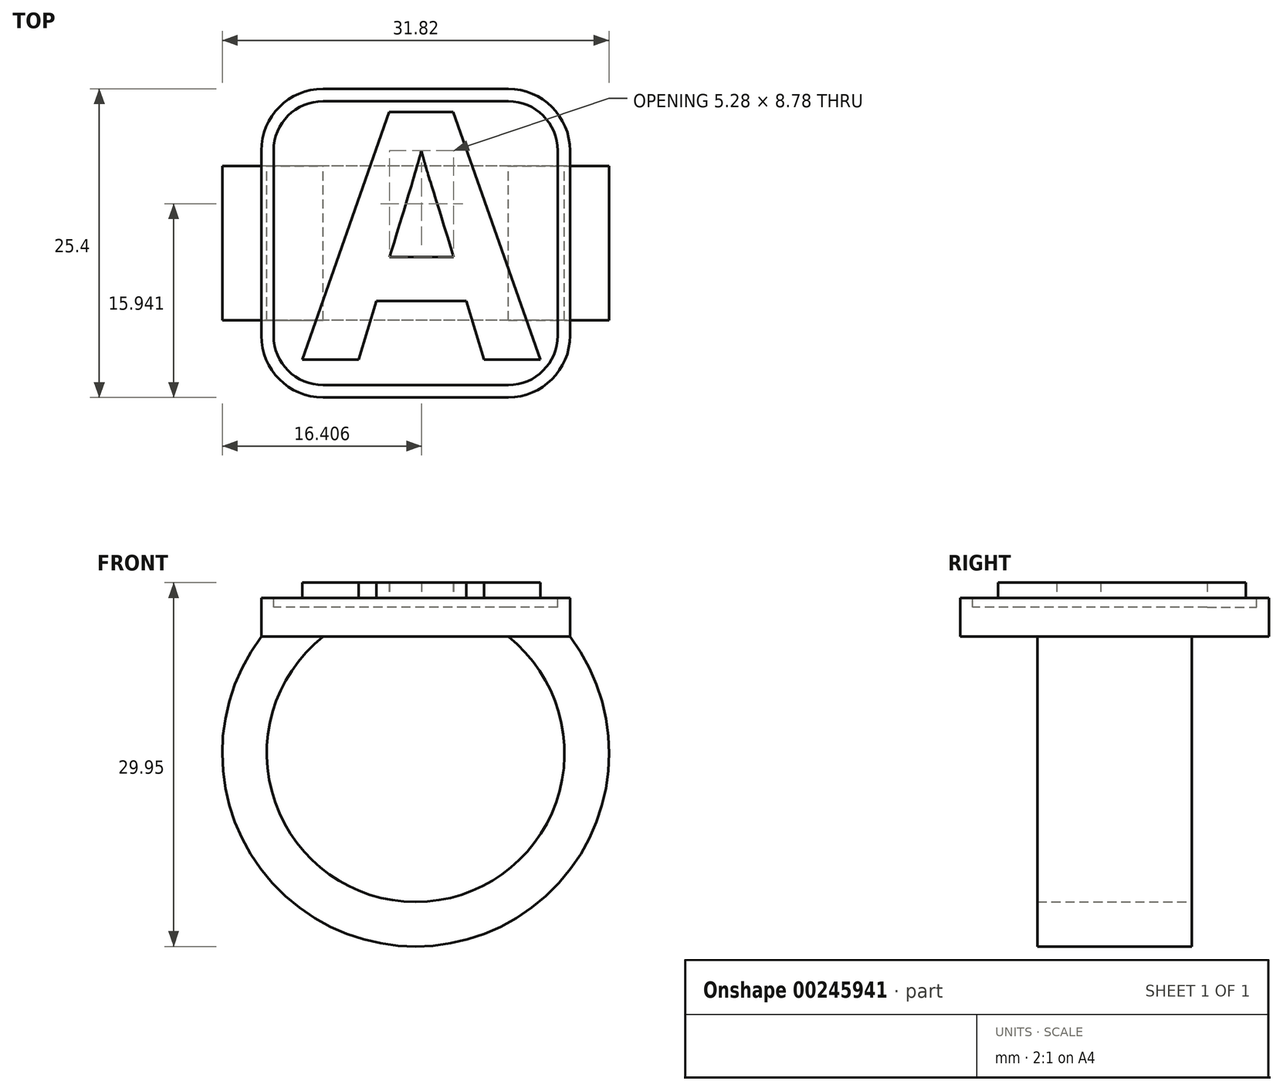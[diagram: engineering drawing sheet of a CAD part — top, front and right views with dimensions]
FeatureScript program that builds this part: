
annotation { "Feature Type Name" : "Feature", "Feature Type Description" : "" }
export const myFeature = defineFeature(function(context is Context, id is Id, definition is map)
    precondition{}
    {
        {
            var Q0;
            Q0=qCreatedBy(makeId("Top.planeOp"),FACE);
            var sketch = newSketch(context, id + "F0", { "sketchPlane" : qUnion([Q0])});
            skLineSegment(sketch, "E0.bottom", {"start": v(12.7, 12.7) * mm, "end": v(-12.7, 12.7) * mm});
            skLineSegment(sketch, "E0.top", {"start": v(12.7, -12.7) * mm, "end": v(-12.7, -12.7) * mm});
            skLineSegment(sketch, "E0.left", {"start": v(12.7, 12.7) * mm, "end": v(12.7, -12.7) * mm});
            skLineSegment(sketch, "E0.right", {"start": v(-12.7, 12.7) * mm, "end": v(-12.7, -12.7) * mm});
            skPoint(sketch, "E0.middle", {"position": v(0, 0) * mm});
            skSolve(sketch);
        }
        {
            var Q0;
            Q0=makeQuery(id+"F0.imprint","IMPRINT",FACE,{"disambiguationData":[TD([[makeQuery(id+"F0.imprint","IMPRINT",EDGE,{"derivedFrom":sQuery(id+"F0.wireOp",EDGE,"E0.bottom")}),1.0]])]});
            extrude(context, id + "F1", {"entities" : qUnion([Q0]), "depth" : 3.17 * mm});
        }
        {
            var Q0;
            Q0=qCreatedBy(makeId("Front.planeOp"),FACE);
            var sketch = newSketch(context, id + "F2", { "sketchPlane" : qUnion([Q0])});
            skArc(sketch, "E1", {"start": v(-10.16, 0) * mm, "mid": v(0, -23.56) * mm, "end": v(10.16, 0) * mm});
            skSolve(sketch);
        }
        {
            var Q0;
            Q0=makeQuery(id+"F1.opExtrude","CAP_FACE",FACE,{"disambiguationData":[OSD([sQuery(id+"F0.wireOp",EDGE,"E0.bottom"),sQuery(id+"F0.wireOp",EDGE,"E0.top"),sQuery(id+"F0.wireOp",EDGE,"E0.left"),sQuery(id+"F0.wireOp",EDGE,"E0.right")])],"isStart":true});
            var sketch = newSketch(context, id + "F3", { "sketchPlane" : qUnion([Q0])});
            skLineSegment(sketch, "E2.bottom", {"start": v(7.62, 6.35) * mm, "end": v(12.7, 6.35) * mm});
            skLineSegment(sketch, "E2.top", {"start": v(7.62, -6.35) * mm, "end": v(12.7, -6.35) * mm});
            skLineSegment(sketch, "E2.left", {"start": v(7.62, 6.35) * mm, "end": v(7.62, -6.35) * mm});
            skLineSegment(sketch, "E2.right", {"start": v(12.7, 6.35) * mm, "end": v(12.7, -6.35) * mm});
            skPoint(sketch, "E2.middle", {"position": v(10.16, 0) * mm});
            skSolve(sketch);
        }
        {
            var Q0;
            Q0 = qSketchRegion(id + "F3", true);
            var Q1;
            Q1 = qConstructionFilter(qBodyType(qCreatedBy(id + "F2" ,EDGE), BodyType.WIRE), ConstructionObject.NO);
            sweep(context, id + "F4", {"operationType" : NewBodyOperationType.ADD, "profiles" : qUnion([Q0]), "path" : qUnion([Q1])});
        }
        {
            var Q0;
            Q0=qCreatedBy(makeId("Front.planeOp"),FACE);
            var sketch = newSketch(context, id + "F5", { "sketchPlane" : qUnion([Q0])});
            skArc(sketch, "E3", {"start": v(-7.62, 0) * mm, "mid": v(-8.9, -1.18) * mm, "end": v(-10.01, -2.54) * mm});
            skLineSegment(sketch, "E4.0", {"start": v(-7.62, 0) * mm, "end": v(-10.16, 0) * mm});
            skLineSegment(sketch, "E5.0", {"start": v(-10.16, 0) * mm, "end": v(-10.01, -2.54) * mm});
            skPoint(sketch, "E6.orphan", {"position": v(-12.7, 0) * mm});
            skPoint(sketch, "E7.orphan", {"position": v(12.7, 0) * mm});
            skSolve(sketch);
        }
        {
            var Q0;
            Q0 = qSketchRegion(id + "F5", true);
            extrude(context, id + "F6", {"entities" : qUnion([Q0]), "operationType" : NewBodyOperationType.ADD, "endBound" : BoundingType.SYMMETRIC, "depth" : 12.7 * mm});
        }
        {
            var Q0;
            Q0=makeQuery(id+"F1.opExtrude","SWEPT_EDGE",EDGE,{"disambiguationData":[OSD([sQuery(id+"F0.wireOp",EDGE,"E0.top"),sQuery(id+"F0.wireOp",EDGE,"E0.left")])]});
            var Q1;
            Q1=makeQuery(id+"F1.opExtrude","SWEPT_EDGE",EDGE,{"disambiguationData":[OSD([sQuery(id+"F0.wireOp",EDGE,"E0.top"),sQuery(id+"F0.wireOp",EDGE,"E0.right")])]});
            var Q2;
            Q2=makeQuery(id+"F1.opExtrude","SWEPT_EDGE",EDGE,{"disambiguationData":[OSD([sQuery(id+"F0.wireOp",EDGE,"E0.bottom"),sQuery(id+"F0.wireOp",EDGE,"E0.left")])]});
            var Q3;
            Q3=makeQuery(id+"F1.opExtrude","SWEPT_EDGE",EDGE,{"disambiguationData":[OSD([sQuery(id+"F0.wireOp",EDGE,"E0.bottom"),sQuery(id+"F0.wireOp",EDGE,"E0.right")])]});
            fillet(context, id + "F7", {"entities" : qUnion([Q0, Q1, Q2, Q3]), "radius" : 5.08 * mm, "tangentPropagation" : true, "allowEdgeOverflow" : false});
        }
        {
            var Q0;
            Q0=makeQuery(id+"F1.opExtrude","CAP_FACE",FACE,{"disambiguationData":[OSD([sQuery(id+"F0.wireOp",EDGE,"E0.bottom"),sQuery(id+"F0.wireOp",EDGE,"E0.top"),sQuery(id+"F0.wireOp",EDGE,"E0.left"),sQuery(id+"F0.wireOp",EDGE,"E0.right")])],"isStart":false});
            var sketch = newSketch(context, id + "F8", { "sketchPlane" : qUnion([Q0])});
            skSolve(sketch);
        }
        {
            var Q0;
            {var subQ3=sQuery(id+"F0.wireOp",EDGE,"E0.bottom");Q0=makeQuery(id+"F8.imprint","IMPRINT",FACE,{"disambiguationData":[TD([[makeQuery(id+"F8.imprint","IMPRINT",EDGE,{"derivedFrom":makeQuery(id+"F1.opExtrude","CAP_EDGE",EDGE,{"disambiguationData":[OSD([subQ3])],"isStart":false})}),1.0]])]});}
            var sketch = newSketch(context, id + "F9", { "sketchPlane" : qUnion([Q0])});
            skLineSegment(sketch, "E8.0", {"start": v(7.62, 11.68) * mm, "end": v(-7.62, 11.68) * mm});
            skArc(sketch, "E8.1", {"start": v(11.68, 7.62) * mm, "mid": v(10.5, 10.5) * mm, "end": v(7.62, 11.68) * mm});
            skArc(sketch, "E8.2", {"start": v(-7.62, 11.68) * mm, "mid": v(-10.5, 10.5) * mm, "end": v(-11.68, 7.62) * mm});
            skLineSegment(sketch, "E8.3", {"start": v(11.68, 7.62) * mm, "end": v(11.68, -7.62) * mm});
            skLineSegment(sketch, "E8.4", {"start": v(-11.68, 7.62) * mm, "end": v(-11.68, -7.62) * mm});
            skArc(sketch, "E8.5", {"start": v(-11.68, -7.62) * mm, "mid": v(-10.5, -10.5) * mm, "end": v(-7.62, -11.68) * mm});
            skLineSegment(sketch, "E8.6", {"start": v(7.62, -11.68) * mm, "end": v(-7.62, -11.68) * mm});
            skArc(sketch, "E8.7", {"start": v(7.62, -11.68) * mm, "mid": v(10.5, -10.5) * mm, "end": v(11.68, -7.62) * mm});
            skSolve(sketch);
        }
        {
            var Q0;
            Q0 = qSketchRegion(id + "F9", true);
            extrude(context, id + "F10", {"entities" : qUnion([Q0]), "operationType" : NewBodyOperationType.REMOVE, "oppositeDirection" : true, "depth" : 0.76 * mm});
        }
        {
            var Q0;
            {var subQ3=sQuery(id+"F0.wireOp",EDGE,"E0.bottom");Q0=makeQuery(id+"F8.imprint","IMPRINT",FACE,{"disambiguationData":[TD([[makeQuery(id+"F8.imprint","IMPRINT",EDGE,{"derivedFrom":makeQuery(id+"F1.opExtrude","CAP_EDGE",EDGE,{"disambiguationData":[OSD([subQ3])],"isStart":false})}),1.0]])]});}
            var sketch = newSketch(context, id + "F11", { "sketchPlane" : qUnion([Q0])});
            skText(sketch, "E9", { "text": "A", "fontName": "OpenSans-Bold.ttf"});
            const initialGuessF11  = {"E9": [-0.00933, -0.00958, 1, 0, 0.02045]};
            skSetInitialGuess(sketch, initialGuessF11);
            skSolve(sketch);
        }
        {
            var Q0;
            Q0 = qSketchRegion(id + "F11", true);
            extrude(context, id + "F12", {"entities" : qUnion([Q0]), "depth" : 1.27 * mm});
        }
    });
